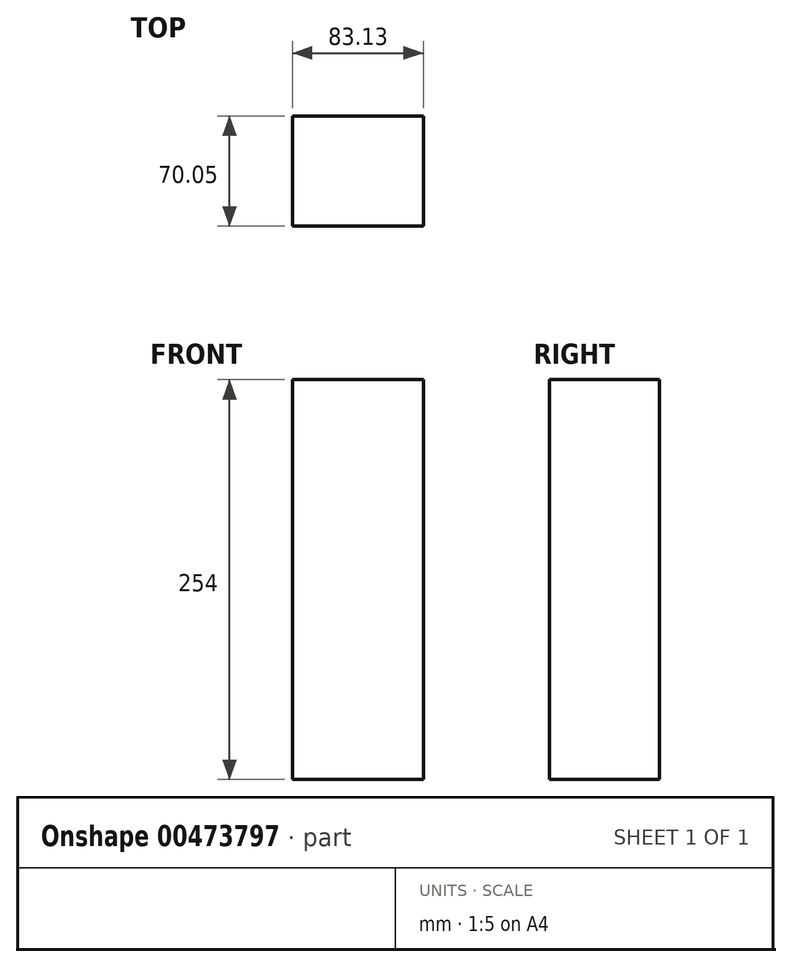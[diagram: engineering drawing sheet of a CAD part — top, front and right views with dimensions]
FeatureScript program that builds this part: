
annotation { "Feature Type Name" : "Feature", "Feature Type Description" : "" }
export const myFeature = defineFeature(function(context is Context, id is Id, definition is map)
    precondition{}
    {
        {
            var Q0;
            Q0=qCreatedBy(makeId("Top.planeOp"),FACE);
            var sketch = newSketch(context, id + "F0", { "sketchPlane" : qUnion([Q0])});
            skLineSegment(sketch, "E0.bottom", {"start": v(-41.4, 30.82) * mm, "end": v(41.72, 30.82) * mm});
            skLineSegment(sketch, "E0.top", {"start": v(-41.4, -39.23) * mm, "end": v(41.72, -39.23) * mm});
            skLineSegment(sketch, "E0.left", {"start": v(-41.4, 30.82) * mm, "end": v(-41.4, -39.23) * mm});
            skLineSegment(sketch, "E0.right", {"start": v(41.72, 30.82) * mm, "end": v(41.72, -39.23) * mm});
            skSolve(sketch);
        }
        {
            var Q0;
            Q0=makeQuery(id+"F0.imprint","IMPRINT",FACE,{"disambiguationData":[TD([[makeQuery(id+"F0.imprint","IMPRINT",EDGE,{"derivedFrom":sQuery(id+"F0.wireOp",EDGE,"E0.bottom")}),-1.0]])]});
            extrude(context, id + "F1", {"entities" : qUnion([Q0]), "depth" : 254 * mm});
        }
    });
